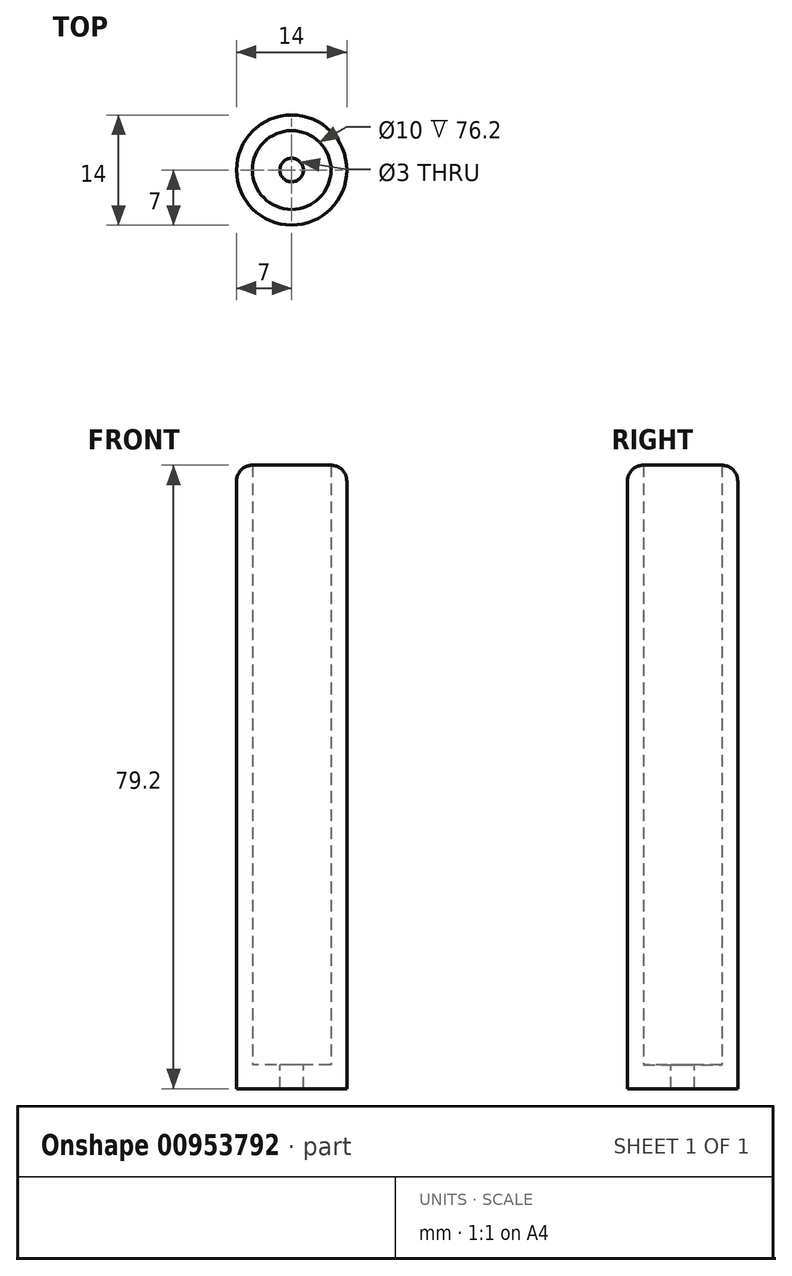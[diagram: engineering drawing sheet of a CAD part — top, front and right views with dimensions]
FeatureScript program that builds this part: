
annotation { "Feature Type Name" : "Feature", "Feature Type Description" : "" }
export const myFeature = defineFeature(function(context is Context, id is Id, definition is map)
    precondition{}
    {
        {
            var Q0;
            Q0=qCreatedBy(makeId("Top.planeOp"),FACE);
            var sketch = newSketch(context, id + "F0", { "sketchPlane" : qUnion([Q0])});
            skCircle(sketch, "E0", {"center": v(0, 0) * mm, "radius": 1.5 * mm});
            skCircle(sketch, "E1", {"center": v(0, 0) * mm, "radius": 5 * mm});
            skCircle(sketch, "E2.0", {"center": v(0, 0) * mm, "radius": 7 * mm});
            skSolve(sketch);
        }
        {
            var Q0;
            Q0=makeQuery(id+"F0.imprint","IMPRINT",FACE,{"disambiguationData":[TD([[makeQuery(id+"F0.imprint","IMPRINT",EDGE,{"derivedFrom":sQuery(id+"F0.wireOp",EDGE,"E1")}),-1.0]])]});
            extrude(context, id + "F1", {"entities" : qUnion([Q0]), "depth" : 76.2 * mm, "offsetDistance" : 25.4 * mm});
        }
        {
            var Q0;
            Q0=makeQuery(id+"F0.imprint","IMPRINT",FACE,{"disambiguationData":[TD([[makeQuery(id+"F0.imprint","IMPRINT",EDGE,{"derivedFrom":sQuery(id+"F0.wireOp",EDGE,"E1")}),-1.0]])]});
            var Q1;
            Q1=makeQuery(id+"F0.imprint","IMPRINT",FACE,{"disambiguationData":[TD([[makeQuery(id+"F0.imprint","IMPRINT",EDGE,{"derivedFrom":sQuery(id+"F0.wireOp",EDGE,"E0")}),-1.0]])]});
            var Q2;
            Q2=sQuery(id+"F0.wireOp",EDGE,"E0");
            var Q3;
            Q3=sQuery(id+"F0.wireOp",EDGE,"E2.0");
            extrude(context, id + "F2", {"entities" : qUnion([Q0, Q1]), "operationType" : NewBodyOperationType.ADD, "surfaceEntities" : qUnion([Q2, Q3]), "oppositeDirection" : true, "depth" : 3 * mm, "offsetDistance" : 25.4 * mm});
        }
        {
            var Q0;
            Q0=makeQuery(id+"F1.opExtrude","CAP_EDGE",EDGE,{"disambiguationData":[OSD([sQuery(id+"F0.wireOp",EDGE,"E2.0")])],"isStart":false});
            fillet(context, id + "F3", {"entities" : qUnion([Q0]), "radius" : 2 * mm, "tangentPropagation" : true, "allowEdgeOverflow" : false});
        }
    });
